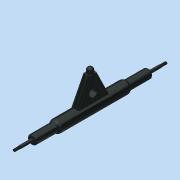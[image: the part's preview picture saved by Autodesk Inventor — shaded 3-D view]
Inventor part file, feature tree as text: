
AUTODESK INVENTOR PART (.ipt)
format: ipt  version: 2015 (Build 190159000, 159)  size: 1,393,664 bytes
history: native  units: in
note: dims shown in document units (in); Inventor stores cm internally (conversion verified against a paired STEP export)
features: plane x6, other x3, imported_body x2
ambient origin geometry x8: Origin, YZ Plane, XZ Plane, XY Plane, X Axis, Y Axis, Z Axis, Center Point
bodies: Body1 (feature_tree), Body2 (feature_tree)
feature tree (11):
  other  "Paris Trucks"
  other  "Paris Trucks.ipt1"
  plane  "Work Plane1"
  plane  "Work Plane2"
  plane  "Work Plane3"
  plane  "Work Plane4"
  plane  "Work Plane5"
  plane  "Work Plane6"
  other  "Paris Trucks_1"
  imported_body  "Base1"
  imported_body  "Base2"
